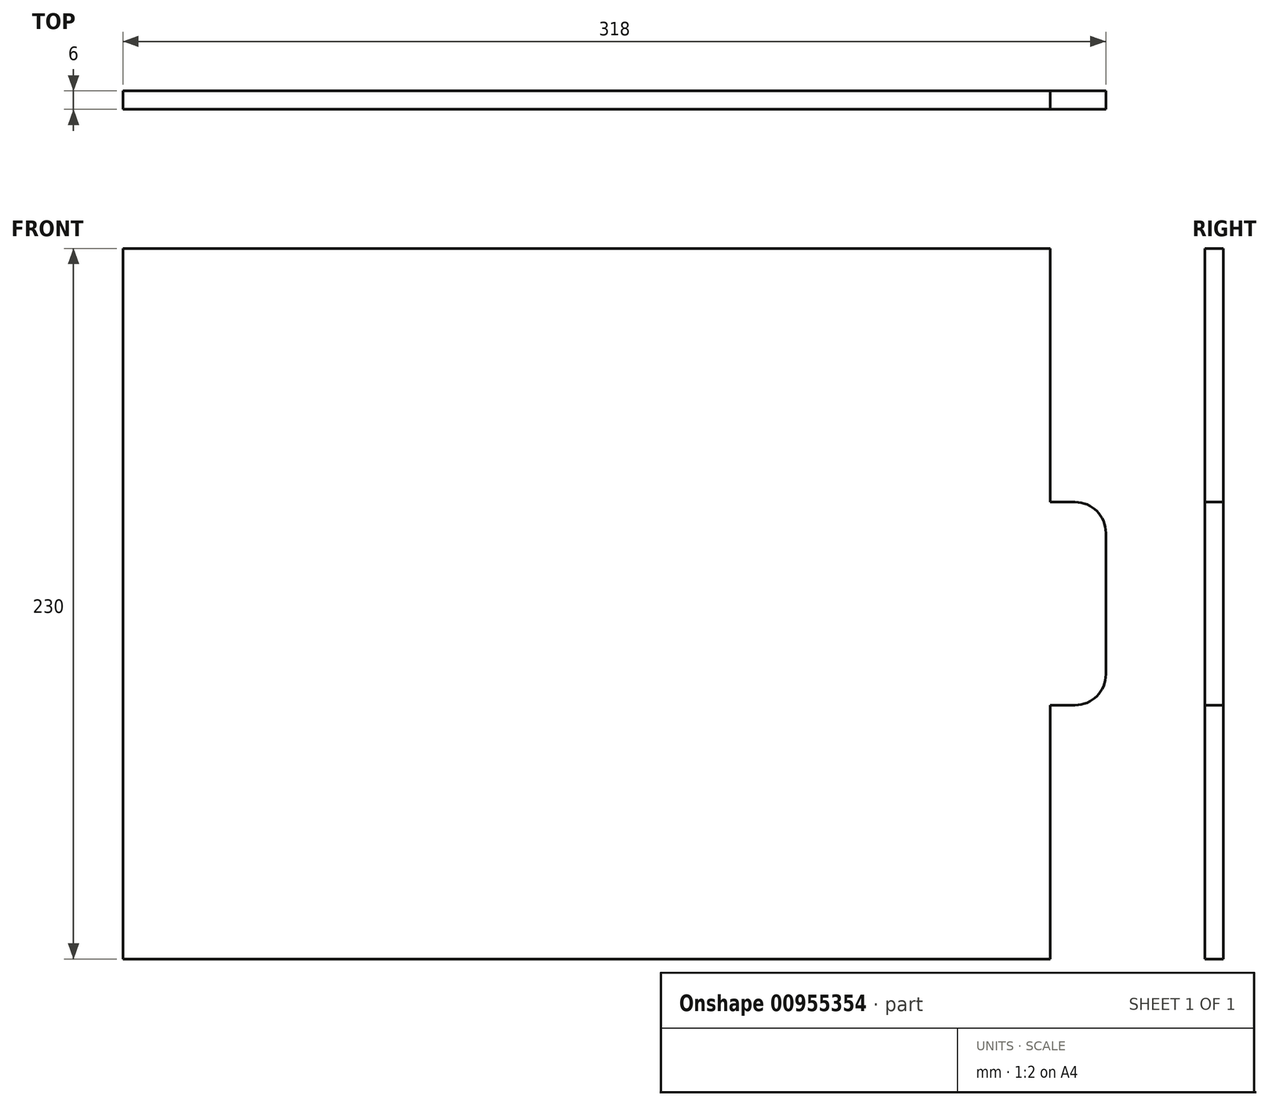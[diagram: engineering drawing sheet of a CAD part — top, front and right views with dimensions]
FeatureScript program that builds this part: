
annotation { "Feature Type Name" : "Feature", "Feature Type Description" : "" }
export const myFeature = defineFeature(function(context is Context, id is Id, definition is map)
    precondition{}
    {
        {
            var Q0;
            Q0=qCreatedBy(makeId("Front.planeOp"),FACE);
            var sketch = newSketch(context, id + "F0", { "sketchPlane" : qUnion([Q0])});
            skLineSegment(sketch, "E0.left", {"start": v(150, -115) * mm, "end": v(150, -32.87) * mm});
            skLineSegment(sketch, "E0.right", {"start": v(-150, -115) * mm, "end": v(-150, 115) * mm});
            skPoint(sketch, "E0.middle", {"position": v(0, 0) * mm});
            skLineSegment(sketch, "E1.bottom", {"start": v(158, -32.87) * mm, "end": v(150, -32.87) * mm});
            skLineSegment(sketch, "E1.top", {"start": v(158, 32.87) * mm, "end": v(150, 32.87) * mm});
            skLineSegment(sketch, "E1.left", {"start": v(168, -22.87) * mm, "end": v(168, 22.87) * mm});
            skPoint(sketch, "E2.visualSharp", {"position": v(168, 32.87) * mm});
            skArc(sketch, "E2.filletArc", {"start": v(168, 22.87) * mm, "mid": v(165.07, 29.94) * mm, "end": v(158, 32.87) * mm});
            skPoint(sketch, "E3.visualSharp", {"position": v(168, -32.87) * mm});
            skArc(sketch, "E3.filletArc", {"start": v(158, -32.87) * mm, "mid": v(165.07, -29.94) * mm, "end": v(168, -22.87) * mm});
            skLineSegment(sketch, "E4.trimOffspring", {"start": v(150, 32.87) * mm, "end": v(150, 115) * mm});
            skLineSegment(sketch, "E5.MirrorCS", {"start": v(-150, 115) * mm, "end": v(-150, -115) * mm});
            skLineSegment(sketch, "E6", {"start": v(-150, 115) * mm, "end": v(150, 115) * mm});
            skLineSegment(sketch, "E7", {"start": v(-150, -115) * mm, "end": v(150, -115) * mm});
            skSolve(sketch);
        }
        {
            var Q0;
            Q0=makeQuery(id+"F0.imprint","IMPRINT",FACE,{"disambiguationData":[TD([[makeQuery(id+"F0.imprint","IMPRINT",EDGE,{"derivedFrom":sQuery(id+"F0.wireOp",EDGE,"E0.left")}),1.0]])]});
            extrude(context, id + "F1", {"entities" : qUnion([Q0]), "depth" : 6 * mm, "offsetDistance" : 25 * mm});
        }
    });
